# Revit family: A307 Bolts-Nut
name_source: partatom
category: Detail Items
revit_build: Autodesk Revit Architecture 2012 (Build: 20110210_1515)
units: mm (PartAtom-declared; Revit-internal decimal feet)

## types (9) — shared parameters
ASTM Designation = A307

## per-type parameters (varying)
| type | D | D2 | F | F1 | F2 | Keynote | r |
| 1/2" | 0.500" | 0.250" | 0.876" | 0.253" | 0.506" | 05 05 23.A1 | 0.438" |
| 5/8" | 0.625" | 0.313" | 1.064" | 0.307" | 0.614" | 05 05 23.A2 | 0.532" |
| 3/4" | 0.750" | 0.375" | 1.250" | 0.361" | 0.722" | 05 05 23.A3 | 0.625" |
| 7/8" | 0.875" | 0.438" | 1.438" | 0.415" | 0.830" | 05 05 23.A4 | 0.719" |
| 1" | 1.000" | 0.500" | 1.625" | 0.469" | 0.938" | 05 05 23.A5 | 0.813" |
| 1 1/8" | 1.125" | 0.563" | 1.814" | 0.524" | 1.047" | 05 05 23.A6 | 0.907" |
| 1 1/4" | 1.250" | 0.625" | 2.000" | 0.577" | 1.155" | 05 05 23.A7 | 1.000" |
| 1 3/8" | 1.375" | 0.688" | 2.188" | 0.632" | 1.263" | 05 05 23.A8 | 1.094" |
| 1 1/2" | 1.500" | 0.750" | 2.376" | 0.686" | 1.372" | 05 05 23.A9 | 1.188" |

## geometry (parser evidence)
native form markers: Sweep x1
no freeform markers — native parametric forms only
